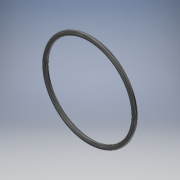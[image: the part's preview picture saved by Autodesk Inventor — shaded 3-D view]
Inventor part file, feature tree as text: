
AUTODESK INVENTOR PART (.ipt)
format: ipt  version: 2018 (Build 220112000, 112)  size: 152,064 bytes
history: native  units: mm (DEFAULTED — no unit token found)
features: revolve x1, sketch x1
ambient origin geometry x8: Origin, YZ Plane, XZ Plane, XY Plane, X Axis, Y Axis, Z Axis, Center Point
bodies: Solid1 (feature_tree)
feature tree (2):
  revolve  "Revolution1"  [1 undecoded]
  sketch  "Sketch1"  dims[d0=3.0mm d1=61.0mm d2=90.0deg]
note: 1 required parameter value undecoded (feature->parameter linkage not recoverable at this tier; creation-order binding heuristic only, values carry confidence <= 0.55)
